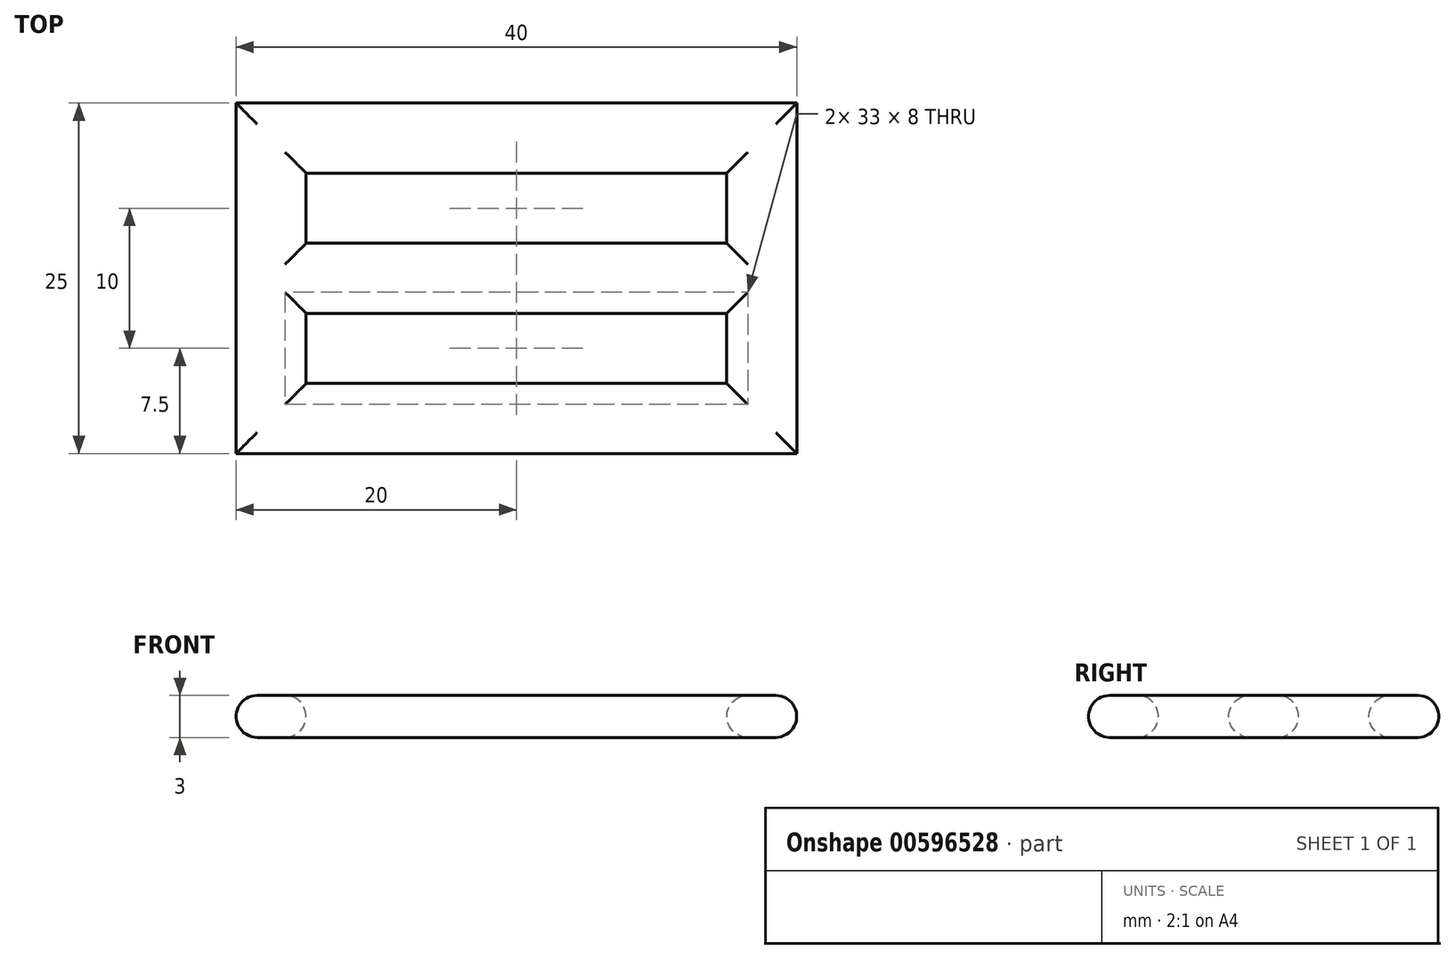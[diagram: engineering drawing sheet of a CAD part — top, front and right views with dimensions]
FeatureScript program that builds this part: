
annotation { "Feature Type Name" : "Feature", "Feature Type Description" : "" }
export const myFeature = defineFeature(function(context is Context, id is Id, definition is map)
    precondition{}
    {
        {
            var Q0;
            Q0=qCreatedBy(makeId("Top.planeOp"),FACE);
            var sketch = newSketch(context, id + "F0", { "sketchPlane" : qUnion([Q0])});
            skLineSegment(sketch, "E0.bottom", {"start": v(20, 12.5) * mm, "end": v(-20, 12.5) * mm});
            skLineSegment(sketch, "E0.top", {"start": v(20, -12.5) * mm, "end": v(-20, -12.5) * mm});
            skLineSegment(sketch, "E0.left", {"start": v(20, 12.5) * mm, "end": v(20, -12.5) * mm});
            skLineSegment(sketch, "E0.right", {"start": v(-20, 12.5) * mm, "end": v(-20, -12.5) * mm});
            skPoint(sketch, "E0.middle", {"position": v(0, 0) * mm});
            skLineSegment(sketch, "E1.bottom", {"start": v(-15, 7.5) * mm, "end": v(15, 7.5) * mm});
            skLineSegment(sketch, "E1.top", {"start": v(-15, 2.5) * mm, "end": v(15, 2.5) * mm});
            skLineSegment(sketch, "E1.left", {"start": v(-15, 7.5) * mm, "end": v(-15, 2.5) * mm});
            skLineSegment(sketch, "E1.right", {"start": v(15, 7.5) * mm, "end": v(15, 2.5) * mm});
            skLineSegment(sketch, "E2.bottom", {"start": v(-15, -2.5) * mm, "end": v(15, -2.5) * mm});
            skLineSegment(sketch, "E2.top", {"start": v(-15, -7.5) * mm, "end": v(15, -7.5) * mm});
            skLineSegment(sketch, "E2.left", {"start": v(-15, -2.5) * mm, "end": v(-15, -7.5) * mm});
            skLineSegment(sketch, "E2.right", {"start": v(15, -2.5) * mm, "end": v(15, -7.5) * mm});
            skSolve(sketch);
        }
        {
            var Q0;
            Q0 = qSketchRegion(id + "F0", true);
            extrude(context, id + "F1", {"entities" : qUnion([Q0]), "depth" : 3 * mm, "offsetDistance" : 25.4 * mm});
        }
        {
            var Q0;
            Q0=makeQuery(id+"F1.opExtrude","CAP_EDGE",EDGE,{"disambiguationData":[OSD([sQuery(id+"F0.wireOp",EDGE,"E0.top")])],"isStart":false});
            var Q1;
            Q1=makeQuery(id+"F1.opExtrude","CAP_EDGE",EDGE,{"disambiguationData":[OSD([sQuery(id+"F0.wireOp",EDGE,"E0.right")])],"isStart":false});
            var Q2;
            Q2=makeQuery(id+"F1.opExtrude","CAP_EDGE",EDGE,{"disambiguationData":[OSD([sQuery(id+"F0.wireOp",EDGE,"E0.bottom")])],"isStart":false});
            var Q3;
            Q3=makeQuery(id+"F1.opExtrude","CAP_EDGE",EDGE,{"disambiguationData":[OSD([sQuery(id+"F0.wireOp",EDGE,"E0.left")])],"isStart":false});
            var Q4;
            Q4=makeQuery(id+"F1.opExtrude","CAP_EDGE",EDGE,{"disambiguationData":[OSD([sQuery(id+"F0.wireOp",EDGE,"E0.top")])],"isStart":true});
            var Q5;
            Q5=makeQuery(id+"F1.opExtrude","CAP_EDGE",EDGE,{"disambiguationData":[OSD([sQuery(id+"F0.wireOp",EDGE,"E0.left")])],"isStart":true});
            var Q6;
            Q6=makeQuery(id+"F1.opExtrude","CAP_EDGE",EDGE,{"disambiguationData":[OSD([sQuery(id+"F0.wireOp",EDGE,"E0.right")])],"isStart":true});
            var Q7;
            Q7=makeQuery(id+"F1.opExtrude","CAP_EDGE",EDGE,{"disambiguationData":[OSD([sQuery(id+"F0.wireOp",EDGE,"E0.bottom")])],"isStart":true});
            var Q8;
            Q8=makeQuery(id+"F1.opExtrude","CAP_EDGE",EDGE,{"disambiguationData":[OSD([sQuery(id+"F0.wireOp",EDGE,"E1.top")])],"isStart":false});
            var Q9;
            Q9=makeQuery(id+"F1.opExtrude","CAP_EDGE",EDGE,{"disambiguationData":[OSD([sQuery(id+"F0.wireOp",EDGE,"E1.bottom")])],"isStart":false});
            var Q10;
            Q10=makeQuery(id+"F1.opExtrude","CAP_EDGE",EDGE,{"disambiguationData":[OSD([sQuery(id+"F0.wireOp",EDGE,"E1.right")])],"isStart":false});
            var Q11;
            Q11=makeQuery(id+"F1.opExtrude","CAP_EDGE",EDGE,{"disambiguationData":[OSD([sQuery(id+"F0.wireOp",EDGE,"E2.right")])],"isStart":false});
            var Q12;
            Q12=makeQuery(id+"F1.opExtrude","CAP_EDGE",EDGE,{"disambiguationData":[OSD([sQuery(id+"F0.wireOp",EDGE,"E2.top")])],"isStart":false});
            var Q13;
            Q13=makeQuery(id+"F1.opExtrude","CAP_EDGE",EDGE,{"disambiguationData":[OSD([sQuery(id+"F0.wireOp",EDGE,"E2.bottom")])],"isStart":false});
            var Q14;
            Q14=makeQuery(id+"F1.opExtrude","CAP_EDGE",EDGE,{"disambiguationData":[OSD([sQuery(id+"F0.wireOp",EDGE,"E2.left")])],"isStart":false});
            var Q15;
            Q15=makeQuery(id+"F1.opExtrude","CAP_EDGE",EDGE,{"disambiguationData":[OSD([sQuery(id+"F0.wireOp",EDGE,"E1.left")])],"isStart":false});
            var Q16;
            Q16=makeQuery(id+"F1.opExtrude","CAP_EDGE",EDGE,{"disambiguationData":[OSD([sQuery(id+"F0.wireOp",EDGE,"E1.top")])],"isStart":true});
            var Q17;
            Q17=makeQuery(id+"F1.opExtrude","CAP_EDGE",EDGE,{"disambiguationData":[OSD([sQuery(id+"F0.wireOp",EDGE,"E1.right")])],"isStart":true});
            var Q18;
            Q18=makeQuery(id+"F1.opExtrude","CAP_EDGE",EDGE,{"disambiguationData":[OSD([sQuery(id+"F0.wireOp",EDGE,"E1.bottom")])],"isStart":true});
            var Q19;
            Q19=makeQuery(id+"F1.opExtrude","CAP_EDGE",EDGE,{"disambiguationData":[OSD([sQuery(id+"F0.wireOp",EDGE,"E1.left")])],"isStart":true});
            var Q20;
            Q20=makeQuery(id+"F1.opExtrude","CAP_EDGE",EDGE,{"disambiguationData":[OSD([sQuery(id+"F0.wireOp",EDGE,"E2.left")])],"isStart":true});
            var Q21;
            Q21=makeQuery(id+"F1.opExtrude","CAP_EDGE",EDGE,{"disambiguationData":[OSD([sQuery(id+"F0.wireOp",EDGE,"E2.bottom")])],"isStart":true});
            var Q22;
            Q22=makeQuery(id+"F1.opExtrude","CAP_EDGE",EDGE,{"disambiguationData":[OSD([sQuery(id+"F0.wireOp",EDGE,"E2.right")])],"isStart":true});
            var Q23;
            Q23=makeQuery(id+"F1.opExtrude","CAP_EDGE",EDGE,{"disambiguationData":[OSD([sQuery(id+"F0.wireOp",EDGE,"E2.top")])],"isStart":true});
            fillet(context, id + "F2", {"entities" : qUnion([Q0, Q1, Q2, Q3, Q4, Q5, Q6, Q7, Q8, Q9, Q10, Q11, Q12, Q13, Q14, Q15, Q16, Q17, Q18, Q19, Q20, Q21, Q22, Q23]), "radius" : 1.5 * mm, "tangentPropagation" : true, "allowEdgeOverflow" : false});
        }
    });
